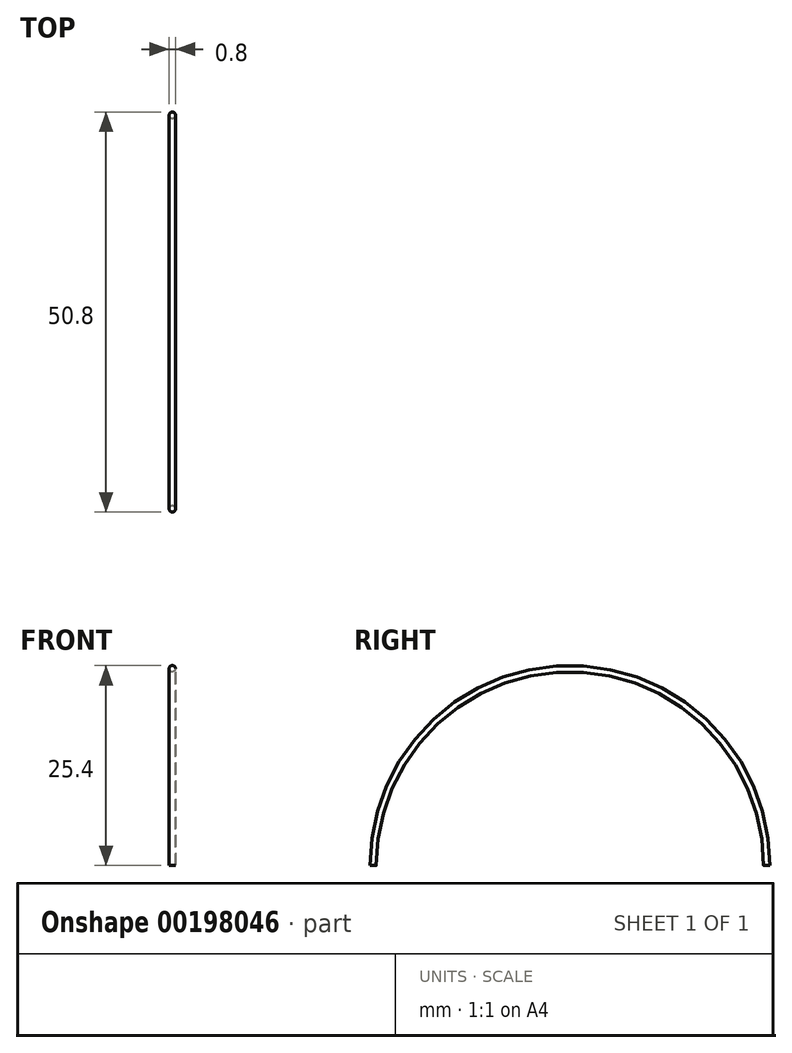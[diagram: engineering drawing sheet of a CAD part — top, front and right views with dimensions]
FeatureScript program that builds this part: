
annotation { "Feature Type Name" : "Feature", "Feature Type Description" : "" }
export const myFeature = defineFeature(function(context is Context, id is Id, definition is map)
    precondition{}
    {
        {
            var Q0;
            Q0=qCreatedBy(makeId("Right.planeOp"),FACE);
            var sketch = newSketch(context, id + "F0", { "sketchPlane" : qUnion([Q0])});
            skArc(sketch, "E0", {"start": v(50, 0) * mm, "mid": v(25, 25) * mm, "end": v(0, 0) * mm});
            skSolve(sketch);
        }
        {
            var Q0;
            Q0=qCreatedBy(makeId("Top.planeOp"),FACE);
            var sketch = newSketch(context, id + "F1", { "sketchPlane" : qUnion([Q0])});
            skCircle(sketch, "E1", {"center": v(0, 0) * mm, "radius": 0.4 * mm});
            skSolve(sketch);
        }
        {
            var Q0;
            Q0=makeQuery(id+"F1.imprint","IMPRINT",FACE,{"disambiguationData":[TD([[makeQuery(id+"F1.imprint","IMPRINT",EDGE,{"derivedFrom":sQuery(id+"F1.wireOp",EDGE,"E1")}),1.0]])]});
            var Q1;
            Q1=sQuery(id+"F0.wireOp",EDGE,"E0");
            var Q2;
            Q2=sQuery(id+"F0.wireOp",EDGE,"04kTBhK5-4qhn-PmDg-9jCr-tDoqSLpTsOeG");
            sweep(context, id + "F2", {"profiles" : qUnion([Q0]), "path" : qUnion([Q1, Q2])});
        }
    });
